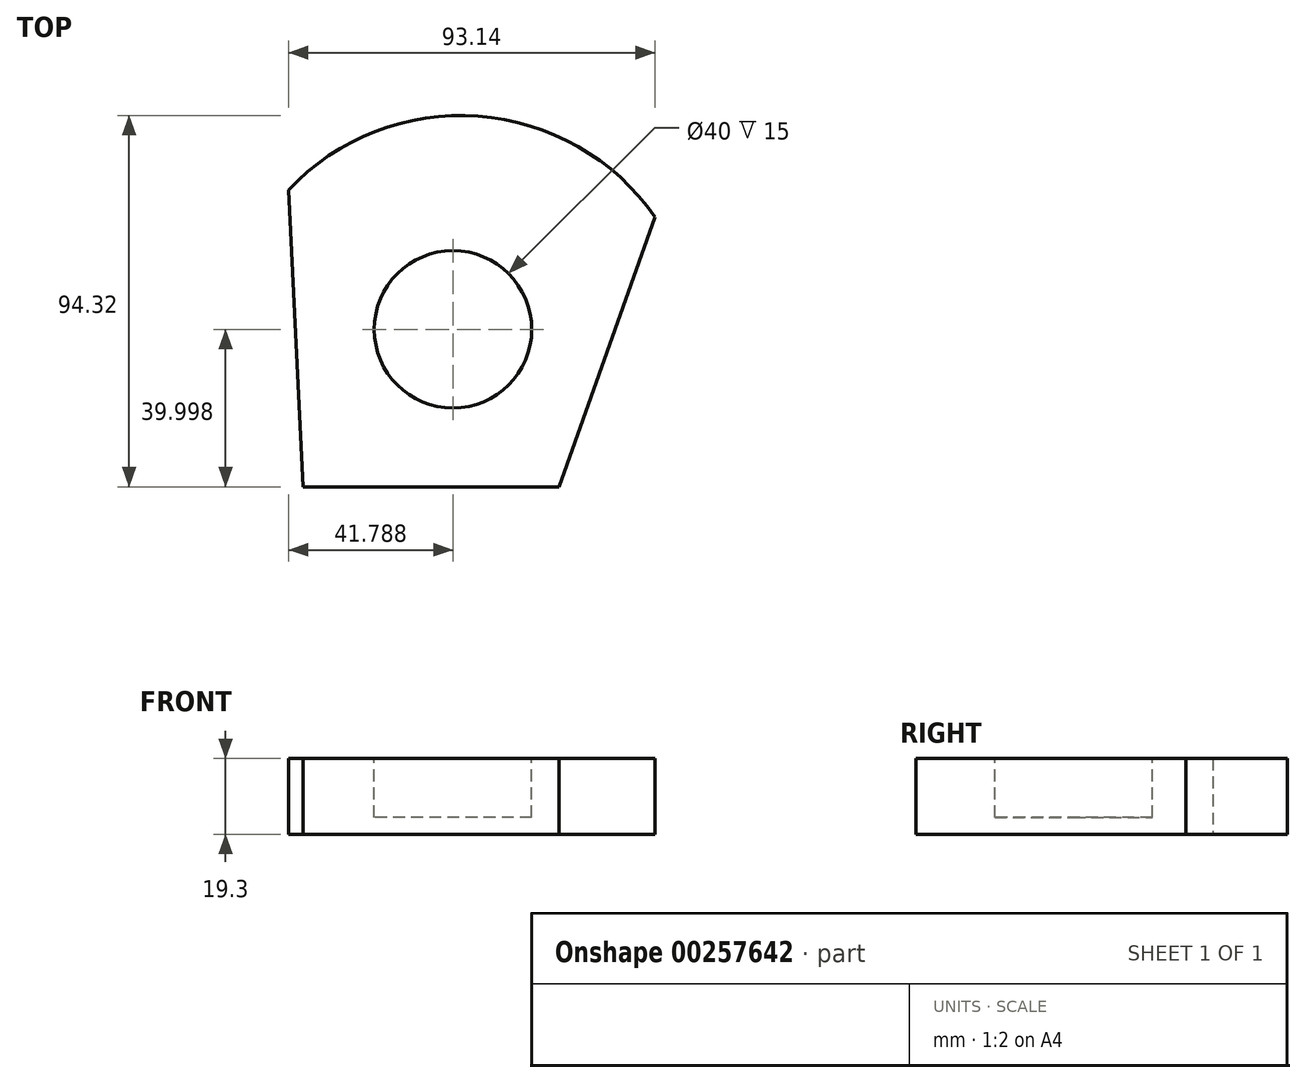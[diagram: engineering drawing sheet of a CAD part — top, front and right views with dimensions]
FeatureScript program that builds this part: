
annotation { "Feature Type Name" : "Feature", "Feature Type Description" : "" }
export const myFeature = defineFeature(function(context is Context, id is Id, definition is map)
    precondition{}
    {
        {
            var Q0;
            Q0=qCreatedBy(makeId("Top.planeOp"),FACE);
            var sketch = newSketch(context, id + "F0", { "sketchPlane" : qUnion([Q0])});
            skLineSegment(sketch, "E0", {"start": v(-41.06, 46.09) * mm, "end": v(-37.35, -29.32) * mm});
            skLineSegment(sketch, "E1", {"start": v(27.67, -29.32) * mm, "end": v(-37.35, -29.32) * mm});
            skLineSegment(sketch, "E2", {"start": v(52.08, 39.23) * mm, "end": v(27.67, -29.32) * mm});
            skArc(sketch, "E3", {"start": v(52.08, 39.23) * mm, "mid": v(7.14, 64.84) * mm, "end": v(-41.06, 46.09) * mm});
            skSolve(sketch);
        }
        {
            var Q0;
            Q0 = qSketchRegion(id + "F0", true);
            extrude(context, id + "F1", {"entities" : qUnion([Q0]), "depth" : 19.3 * mm});
        }
        {
            var Q0;
            Q0=makeQuery(id+"F1.opExtrude","CAP_FACE",FACE,{"disambiguationData":[OSD([sQuery(id+"F0.wireOp",EDGE,"E0"),sQuery(id+"F0.wireOp",EDGE,"E1"),sQuery(id+"F0.wireOp",EDGE,"E2"),sQuery(id+"F0.wireOp",EDGE,"E3")])],"isStart":false});
            var sketch = newSketch(context, id + "F2", { "sketchPlane" : qUnion([Q0])});
            skCircle(sketch, "E4", {"center": v(0.73, 10.68) * mm, "radius": 20 * mm});
            skSolve(sketch);
        }
        {
            var Q0;
            Q0=makeQuery(id+"F2.imprint","IMPRINT",FACE,{"disambiguationData":[TD([[makeQuery(id+"F2.imprint","IMPRINT",EDGE,{"derivedFrom":sQuery(id+"F2.wireOp",EDGE,"E4")}),1.0]])]});
            extrude(context, id + "F3", {"entities" : qUnion([Q0]), "operationType" : NewBodyOperationType.REMOVE, "oppositeDirection" : true, "depth" : 15 * mm});
        }
    });
